# Revit family: Faucet-Handle-KOHLER-Artifacts-K-98068
name_source: partatom
category: Plumbing Fixtures
revit_build: Autodesk Revit 2015 (Build: 20140606_1530(x64)
units: mm (PartAtom-declared; Revit-internal decimal feet)

## types (24) — shared parameters
ADA Compliant = Yes
Assembly Code = D2010
CW Connection = Yes
Cold Water Inlet = Cold Water Inlet
Date Modified = 08/14/2018
Default Elevation = 36"
Drain Included = No
Flow Rate = 0 GPM
HW Connection = Yes
Hot Water Inlet = Hot Water Inlet
Length = 2 1/4"
Manufacturer = KOHLER Co.
MasterFormat 1995 = 15410
MasterFormat 2004 = 22.41.39
Material = Metal Construction
Pressure = 0.00 psi
Product Documentation Link = http://www.us.kohler.com
Product Name = Artifacts
Product Page URL = http://www.us.kohler.com
Spout Reach = 0"
URL = https://www.us.kohler.com
Vent Connection = No
Waste Connection = No
Waste Water Outlet = Waste Water Outlet

## per-type parameters (varying)
| type | Description | Finish | Handle Clearance | Height | Model | T_F | Type | _3 | _3M | _4 | _9M |
| Cross Handle, CP-Polished Chrome | Bathroom sink cross handles | Kohler-Metal-CP-Polished_Chrome | 1 9/16" | 3 1/2" | K-98068-3-CP | 0" | 1 | Yes | No | No | No |
| Cross Handle, SN-Vibrant Polished Nickel | Bathroom sink cross handles | Kohler-Metal-SN-Vibrant_Polished_Nickel | 1 9/16" | 3 1/2" | K-98068-3-SN | 0" | 2 | Yes | No | No | No |
| Cross Handle, BN-Vibrant Brushed Nickel | Bathroom sink cross handles | Kohler-Metal-BN-Vibrant_Brushed_Nickel | 1 9/16" | 3 1/2" | K-98068-3-BN | 0" | 3 | Yes | No | No | No |
| Cross Handle, BV-Vibrant Brushed Bronze | Bathroom sink cross handles | Kohler-Metal-BV-Brushed_Bronze | 1 9/16" | 3 1/2" | K-98068-3-BV | 0" | 4 | Yes | No | No | No |
| Cross Handle, 2BZ-Oil-Rubbed Bronze | Bathroom sink cross handles | Kohler-Metal-2BZ-Oil_Rubbed_Bronze | 1 9/16" | 3 1/2" | K-98068-3-2BZ | 0" | 5 | Yes | No | No | No |
| Cross Handle, VNT-Vintage Nickel | Bathroom sink cross handles | Kohler-Metal-VNT-Vintage_Nickel | 1 9/16" | 3 1/2" | K-98068-3-VNT | 0" | 6 | Yes | No | No | No |
| Lever Handle, CP-Polished Chrome | Bathroom sink lever handles | Kohler-Metal-CP-Polished_Chrome | 3 5/16" | 3 5/8" | K-98068-4-CP | 5" | 7 | No | No | Yes | No |
| Lever Handle, SN-Vibrant Polished Nickel | Bathroom sink lever handles | Kohler-Metal-SN-Vibrant_Polished_Nickel | 3 5/16" | 3 5/8" | K-98068-4-SN | 5" | 8 | No | No | Yes | No |
| Lever Handle, BN-Vibrant Brushed Nickel | Bathroom sink lever handles | Kohler-Metal-BN-Vibrant_Brushed_Nickel | 3 5/16" | 3 5/8" | K-98068-4-BN | 5" | 9 | No | No | Yes | No |
| Lever Handle, BV-Vibrant Brushed Bronze | Bathroom sink lever handles | Kohler-Metal-BV-Brushed_Bronze | 3 5/16" | 3 5/8" | K-98068-4-BV | 5" | 10 | No | No | Yes | No |
| Lever Handle, 2BZ-Oil-Rubbed Bronze | Bathroom sink lever handles | Kohler-Metal-2BZ-Oil_Rubbed_Bronze | 3 5/16" | 3 5/8" | K-98068-4-2BZ | 5" | 11 | No | No | Yes | No |
| Lever Handle, VNT-Vintage Nickel | Bathroom sink lever handles | Kohler-Metal-VNT-Vintage_Nickel | 3 5/16" | 3 5/8" | K-98068-4-VNT | 5" | 12 | No | No | Yes | No |
| Prong Handle, CP-Polished Chrome | Bathroom sink prong handles | Kohler-Metal-CP-Polished_Chrome | 1 3/8" | 3 9/16" | K-98068-3M-CP | 10" | 13 | No | Yes | No | No |
| Prong Handle, SN-Vibrant Polished Nickel | Bathroom sink prong handles | Kohler-Metal-SN-Vibrant_Polished_Nickel | 1 3/8" | 3 9/16" | K-98068-3M-SN | 10" | 14 | No | Yes | No | No |
| Prong Handle, BN-Vibrant Brushed Nickel | Bathroom sink prong handles | Kohler-Metal-BN-Vibrant_Brushed_Nickel | 1 3/8" | 3 9/16" | K-98068-3M-BN | 10" | 15 | No | Yes | No | No |
| Prong Handle, BV-Vibrant Brushed Bronze | Bathroom sink prong handles | Kohler-Metal-BV-Brushed_Bronze | 1 3/8" | 3 9/16" | K-98068-3M-BV | 10" | 16 | No | Yes | No | No |
| Prong Handle, 2BZ-Oil-Rubbed Bronze | Bathroom sink prong handles | Kohler-Metal-2BZ-Oil_Rubbed_Bronze | 1 3/8" | 3 9/16" | K-98068-3M-2BZ | 10" | 17 | No | Yes | No | No |
| Prong Handle, VNT-Vintage Nickel | Bathroom sink prong handles | Kohler-Metal-VNT-Vintage_Nickel | 1 3/8" | 3 9/16" | K-98068-3M-VNT | 10" | 18 | No | Yes | No | No |
| Swing lever handles, CP-Polished Chrome | Bathroom sink swing lever handles | Kohler-Metal-CP-Polished_Chrome | 2 1/16" | 4 3/16" | K-98068-9M-CP | 15" | 19 | No | No | No | Yes |
| Swing lever handles, SN-Vibrant Polished Nickel | Bathroom sink swing lever handles | Kohler-Metal-SN-Vibrant_Polished_Nickel | 2 1/16" | 4 3/16" | K-98068-9M-SN | 15" | 20 | No | No | No | Yes |
| Swing lever handles, BN-Vibrant Brushed Nickel | Bathroom sink swing lever handles | Kohler-Metal-BN-Vibrant_Brushed_Nickel | 2 1/16" | 4 3/16" | K-98068-9M-BN | 15" | 21 | No | No | No | Yes |
| Swing lever handles, BV-Vibrant Brushed Bronze | Bathroom sink swing lever handles | Kohler-Metal-BV-Brushed_Bronze | 2 1/16" | 4 3/16" | K-98068-9M-BV | 15" | 22 | No | No | No | Yes |
| Swing lever handles, 2BZ-Oil-Rubbed Bronze | Bathroom sink swing lever handles | Kohler-Metal-2BZ-Oil_Rubbed_Bronze | 2 1/16" | 4 3/16" | K-98068-9M-2BZ | 15" | 23 | No | No | No | Yes |
| Swing lever handles, VNT-Vintage Nickel | Bathroom sink swing lever handles | Kohler-Metal-VNT-Vintage_Nickel | 2 1/16" | 4 3/16" | K-98068-9M-VNT | 15" | 24 | No | No | No | Yes |

## geometry (parser evidence)
native form markers: Sweep x3
no freeform markers — native parametric forms only
